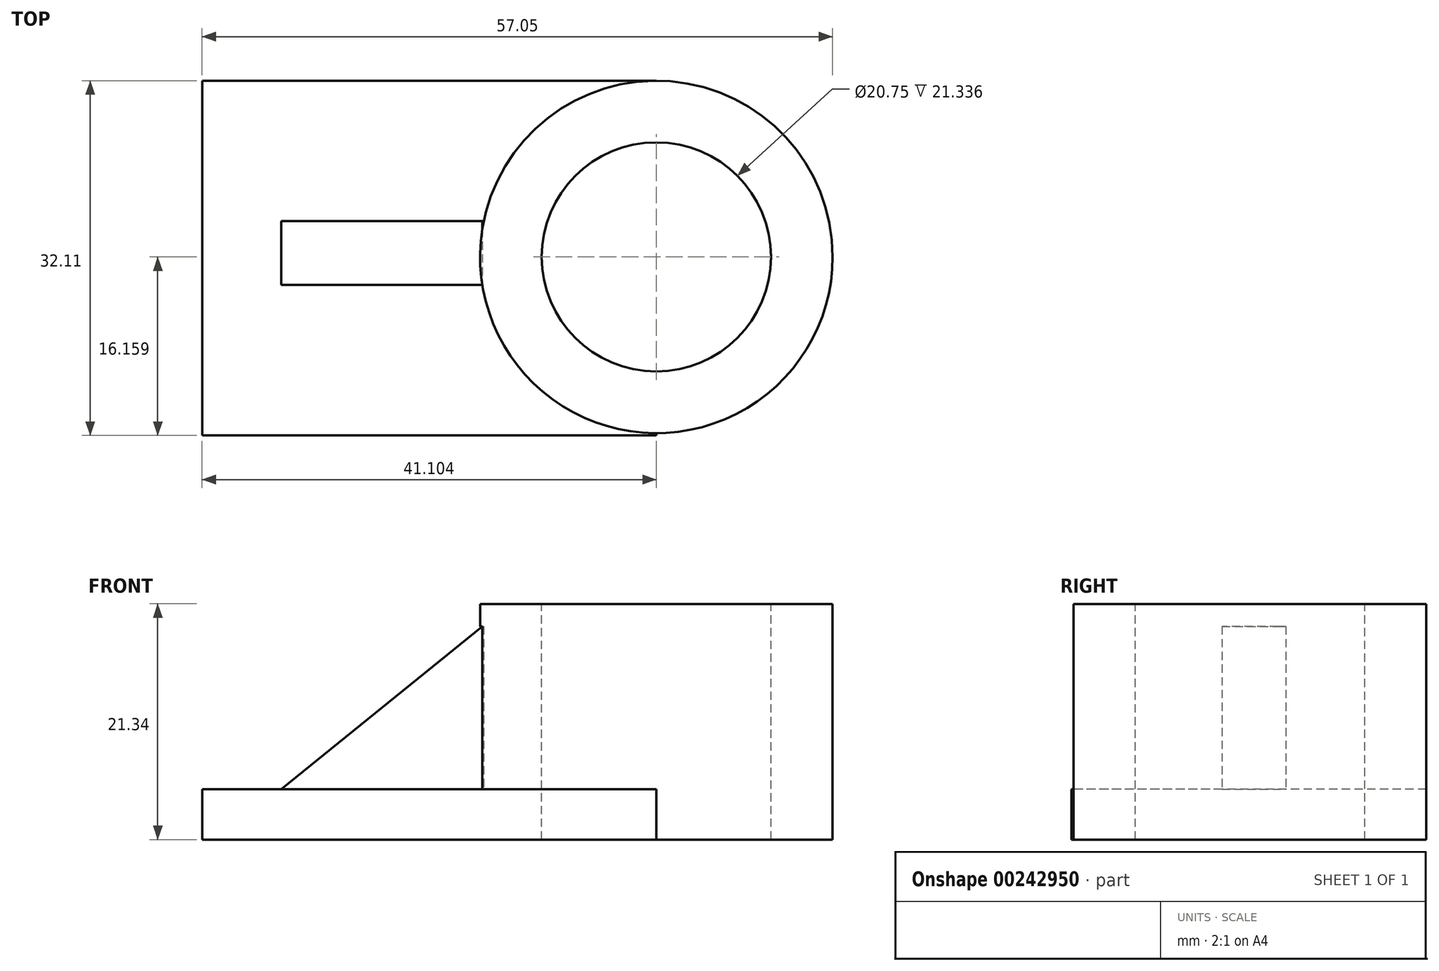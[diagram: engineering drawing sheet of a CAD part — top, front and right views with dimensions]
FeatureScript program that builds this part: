
annotation { "Feature Type Name" : "Feature", "Feature Type Description" : "" }
export const myFeature = defineFeature(function(context is Context, id is Id, definition is map)
    precondition{}
    {
        {
            var Q0;
            Q0=qCreatedBy(makeId("Top.planeOp"),FACE);
            var sketch = newSketch(context, id + "F0", { "sketchPlane" : qUnion([Q0])});
            skCircle(sketch, "E0", {"center": v(31.4, 31.52) * mm, "radius": 15.95 * mm});
            skSolve(sketch);
        }
        {
            var Q0;
            Q0=makeQuery(id+"F0.imprint","IMPRINT",FACE,{"disambiguationData":[TD([[makeQuery(id+"F0.imprint","IMPRINT",EDGE,{"derivedFrom":sQuery(id+"F0.wireOp",EDGE,"E0")}),1.0]])]});
            extrude(context, id + "F1", {"entities" : qUnion([Q0]), "depth" : 21.34 * mm});
        }
        {
            var Q0;
            Q0=makeQuery(id+"F1.opExtrude","CAP_FACE",FACE,{"disambiguationData":[OSD([sQuery(id+"F0.wireOp",EDGE,"E0")])],"isStart":false});
            var sketch = newSketch(context, id + "F2", { "sketchPlane" : qUnion([Q0])});
            skCircle(sketch, "E1", {"center": v(31.4, 31.52) * mm, "radius": 10.37 * mm});
            skSolve(sketch);
        }
        {
            var Q0;
            Q0=makeQuery(id+"F1.opExtrude","CAP_FACE",FACE,{"disambiguationData":[OSD([sQuery(id+"F0.wireOp",EDGE,"E0")])],"isStart":true});
            var sketch = newSketch(context, id + "F3", { "sketchPlane" : qUnion([Q0])});
            skLineSegment(sketch, "E2", {"start": v(31.4, -31.52) * mm, "end": v(31.4, -47.47) * mm});
            skLineSegment(sketch, "E3.bottom", {"start": v(31.4, -47.47) * mm, "end": v(-9.7, -47.47) * mm});
            skLineSegment(sketch, "E3.top", {"start": v(31.4, -15.36) * mm, "end": v(-9.7, -15.36) * mm});
            skLineSegment(sketch, "E3.left", {"start": v(31.4, -47.47) * mm, "end": v(31.4, -15.36) * mm});
            skLineSegment(sketch, "E3.right", {"start": v(-9.7, -47.47) * mm, "end": v(-9.7, -15.36) * mm});
            skSolve(sketch);
        }
        {
            var Q0;
            {var subQ0=sQuery(id+"F3.wireOp",EDGE,"E3.bottom");Q0=makeQuery(id+"F3.imprint","IMPRINT",FACE,{"disambiguationData":[TD([[makeQuery(id+"F3.imprint","IMPRINT",EDGE,{"derivedFrom":subQ0}),-1.0]])]});}
            extrude(context, id + "F4", {"entities" : qUnion([Q0]), "operationType" : NewBodyOperationType.ADD, "oppositeDirection" : true, "depth" : 4.57 * mm});
        }
        {
            var Q0;
            {var subQ0=sQuery(id+"F0.wireOp",EDGE,"E0");Q0=makeQuery(id+"F4.boolean.opBoolean","MERGE",FACE,{"derivedFrom":[makeQuery(id+"F1.opExtrude","CAP_FACE",FACE,{"disambiguationData":[OSD([subQ0])],"isStart":true}),makeQuery(id+"F4.opExtrude","CAP_FACE",FACE,{"disambiguationData":[OSD([subQ0,sQuery(id+"F3.wireOp",EDGE,"E3.bottom"),sQuery(id+"F3.wireOp",EDGE,"E3.top"),sQuery(id+"F3.wireOp",EDGE,"E3.left"),sQuery(id+"F3.wireOp",EDGE,"E3.right")])],"isStart":true})]});}
            var sketch = newSketch(context, id + "F5", { "sketchPlane" : qUnion([Q0])});
            skLineSegment(sketch, "E4.bottom", {"start": v(21.01, -28.98) * mm, "end": v(-2.54, -28.98) * mm});
            skLineSegment(sketch, "E4.top", {"start": v(21.01, -34.75) * mm, "end": v(-2.54, -34.75) * mm});
            skLineSegment(sketch, "E4.left", {"start": v(21.01, -28.98) * mm, "end": v(21.01, -34.75) * mm});
            skLineSegment(sketch, "E4.right", {"start": v(-2.54, -28.98) * mm, "end": v(-2.54, -34.75) * mm});
            skSolve(sketch);
        }
        {
            var Q0;
            Q0=makeQuery(id+"F5.imprint","IMPRINT",FACE,{"disambiguationData":[TD([[makeQuery(id+"F5.imprint","IMPRINT",EDGE,{"derivedFrom":sQuery(id+"F5.wireOp",EDGE,"E4.bottom")}),1.0]])]});
            extrude(context, id + "F6", {"entities" : qUnion([Q0]), "operationType" : NewBodyOperationType.ADD, "oppositeDirection" : true, "depth" : 19.3 * mm});
        }
        {
            var Q0;
            Q0=makeQuery(id+"F6.opExtrude","SWEPT_FACE",FACE,{"disambiguationData":[OSD([sQuery(id+"F5.wireOp",EDGE,"E4.bottom")])]});
            var sketch = newSketch(context, id + "F7", { "sketchPlane" : qUnion([Q0])});
            skLineSegment(sketch, "E5", {"start": v(-2.54, 4.57) * mm, "end": v(15.66, 19.3) * mm});
            skLineSegment(sketch, "E6", {"start": v(15.66, 19.3) * mm, "end": v(-2.54, 19.3) * mm});
            skLineSegment(sketch, "E7", {"start": v(-2.54, 19.3) * mm, "end": v(-2.54, 4.57) * mm});
            skSolve(sketch);
        }
        {
            var Q0;
            Q0=qSketchRegion(id+"F7",true);
            extrude(context, id + "F8", {"entities" : qUnion([Q0]), "operationType" : NewBodyOperationType.REMOVE, "oppositeDirection" : true, "depth" : 62.23 * mm});
        }
        {
            var Q0;
            Q0=makeQuery(id+"F2.imprint","IMPRINT",FACE,{"disambiguationData":[TD([[makeQuery(id+"F2.imprint","IMPRINT",EDGE,{"derivedFrom":sQuery(id+"F2.wireOp",EDGE,"E1")}),1.0]])]});
            extrude(context, id + "F9", {"entities" : qUnion([Q0]), "operationType" : NewBodyOperationType.REMOVE, "oppositeDirection" : true, "depth" : 47 * mm});
        }
    });
